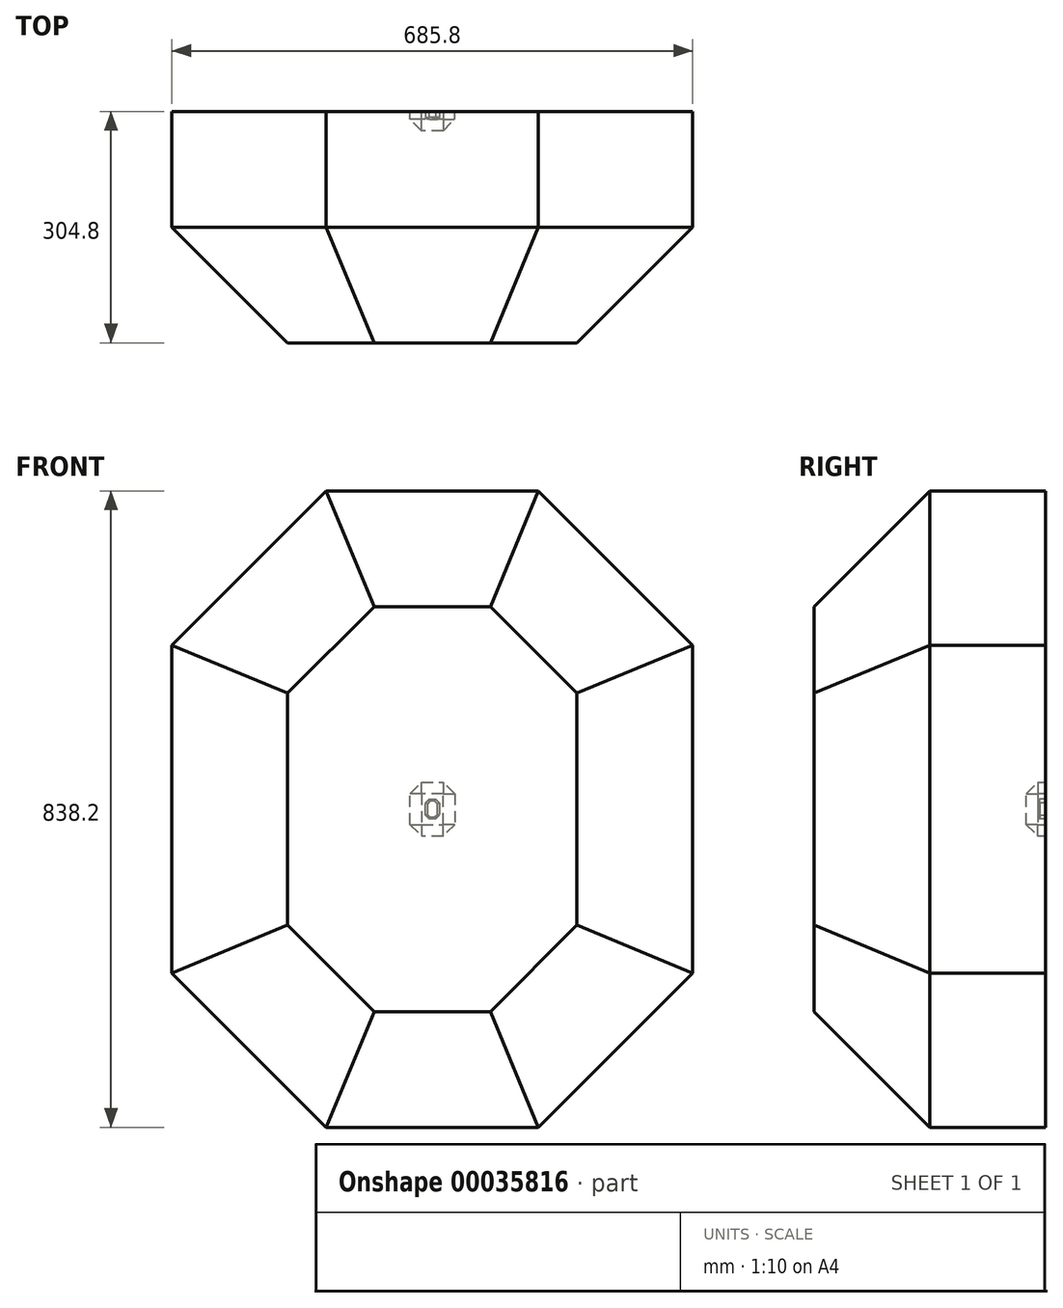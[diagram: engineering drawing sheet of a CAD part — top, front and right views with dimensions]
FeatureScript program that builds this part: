
annotation { "Feature Type Name" : "Feature", "Feature Type Description" : "" }
export const myFeature = defineFeature(function(context is Context, id is Id, definition is map)
    precondition{}
    {
        {
            var Q0;
            Q0=qCreatedBy(makeId("Front.planeOp"),FACE);
            var sketch = newSketch(context, id + "F0", { "sketchPlane" : qUnion([Q0])});
            skLineSegment(sketch, "E0.rect.bottom", {"start": v(29.36, -35.59) * mm, "end": v(-29.36, -35.59) * mm});
            skLineSegment(sketch, "E0.rect.top", {"start": v(29.36, 35.59) * mm, "end": v(-29.36, 35.59) * mm});
            skLineSegment(sketch, "E0.rect.left", {"start": v(29.36, -35.59) * mm, "end": v(29.36, 35.59) * mm});
            skLineSegment(sketch, "E0.rect.right", {"start": v(-29.36, -35.59) * mm, "end": v(-29.36, 35.59) * mm});
            skPoint(sketch, "E0.rect.middle", {"position": v(0, 0) * mm});
            skSolve(sketch);
        }
        {
            var Q0;
            Q0=makeQuery(id+"F0.imprint","IMPRINT",FACE,{"disambiguationData":[TD([[makeQuery(id+"F0.imprint","IMPRINT",EDGE,{"derivedFrom":sQuery(id+"F0.wireOp",EDGE,"E0.rect.bottom")}),-1.0]])]});
            extrude(context, id + "F1", {"entities" : qUnion([Q0]), "depth" : 25.4 * mm});
        }
        {
            var Q0;
            Q0=makeQuery(id+"F1.opExtrude","CAP_FACE",FACE,{"disambiguationData":[OSD([sQuery(id+"F0.wireOp",EDGE,"E0.rect.bottom"),sQuery(id+"F0.wireOp",EDGE,"E0.rect.top"),sQuery(id+"F0.wireOp",EDGE,"E0.rect.left"),sQuery(id+"F0.wireOp",EDGE,"E0.rect.right")])],"isStart":false});
            var Q1;
            Q1=makeQuery(id+"F1.opExtrude","SWEPT_EDGE",EDGE,{"disambiguationData":[OSD([sQuery(id+"F0.wireOp",EDGE,"E0.rect.bottom"),sQuery(id+"F0.wireOp",EDGE,"E0.rect.left")])]});
            var Q2;
            Q2=makeQuery(id+"F1.opExtrude","SWEPT_EDGE",EDGE,{"disambiguationData":[OSD([sQuery(id+"F0.wireOp",EDGE,"E0.rect.bottom"),sQuery(id+"F0.wireOp",EDGE,"E0.rect.right")])]});
            var Q3;
            Q3=makeQuery(id+"F1.opExtrude","SWEPT_EDGE",EDGE,{"disambiguationData":[OSD([sQuery(id+"F0.wireOp",EDGE,"E0.rect.top"),sQuery(id+"F0.wireOp",EDGE,"E0.rect.right")])]});
            var Q4;
            Q4=makeQuery(id+"F1.opExtrude","SWEPT_EDGE",EDGE,{"disambiguationData":[OSD([sQuery(id+"F0.wireOp",EDGE,"E0.rect.top"),sQuery(id+"F0.wireOp",EDGE,"E0.rect.left")])]});
            chamfer(context, id + "F2", {"entities" : qUnion([Q0, Q1, Q2, Q3, Q4]), "width" : 15.24 * mm, "tangentPropagation" : true});
        }
        {
            var Q0;
            Q0=qCreatedBy(makeId("Front.planeOp"),FACE);
            var sketch = newSketch(context, id + "F3", { "sketchPlane" : qUnion([Q0])});
            skLineSegment(sketch, "E1.rect.bottom", {"start": v(342.9, -419.1) * mm, "end": v(-342.9, -419.1) * mm});
            skLineSegment(sketch, "E1.rect.top", {"start": v(342.9, 419.1) * mm, "end": v(-342.9, 419.1) * mm});
            skLineSegment(sketch, "E1.rect.left", {"start": v(342.9, -419.1) * mm, "end": v(342.9, 419.1) * mm});
            skLineSegment(sketch, "E1.rect.right", {"start": v(-342.9, -419.1) * mm, "end": v(-342.9, 419.1) * mm});
            skPoint(sketch, "E1.rect.middle", {"position": v(0, 0) * mm});
            skSolve(sketch);
        }
        {
            var Q0;
            Q0=makeQuery(id+"F3.imprint","IMPRINT",FACE,{"disambiguationData":[TD([[makeQuery(id+"F3.imprint","IMPRINT",EDGE,{"derivedFrom":sQuery(id+"F3.wireOp",EDGE,"E1.rect.bottom")}),-1.0]])]});
            extrude(context, id + "F4", {"entities" : qUnion([Q0]), "depth" : 304.8 * mm});
        }
        {
            var Q0;
            Q0=makeQuery(id+"F4.opExtrude","SWEPT_EDGE",EDGE,{"disambiguationData":[OSD([sQuery(id+"F3.wireOp",EDGE,"E1.rect.top"),sQuery(id+"F3.wireOp",EDGE,"E1.rect.left")])]});
            var Q1;
            Q1=makeQuery(id+"F4.opExtrude","SWEPT_EDGE",EDGE,{"disambiguationData":[OSD([sQuery(id+"F3.wireOp",EDGE,"E1.rect.bottom"),sQuery(id+"F3.wireOp",EDGE,"E1.rect.left")])]});
            var Q2;
            Q2=makeQuery(id+"F4.opExtrude","SWEPT_EDGE",EDGE,{"disambiguationData":[OSD([sQuery(id+"F3.wireOp",EDGE,"E1.rect.bottom"),sQuery(id+"F3.wireOp",EDGE,"E1.rect.right")])]});
            var Q3;
            Q3=makeQuery(id+"F4.opExtrude","SWEPT_EDGE",EDGE,{"disambiguationData":[OSD([sQuery(id+"F3.wireOp",EDGE,"E1.rect.top"),sQuery(id+"F3.wireOp",EDGE,"E1.rect.right")])]});
            chamfer(context, id + "F5", {"entities" : qUnion([Q0, Q1, Q2, Q3]), "width" : 203.2 * mm, "tangentPropagation" : true});
        }
        {
            var Q0;
            Q0=makeQuery(id+"F4.opExtrude","CAP_FACE",FACE,{"disambiguationData":[OSD([sQuery(id+"F3.wireOp",EDGE,"E1.rect.bottom"),sQuery(id+"F3.wireOp",EDGE,"E1.rect.top"),sQuery(id+"F3.wireOp",EDGE,"E1.rect.left"),sQuery(id+"F3.wireOp",EDGE,"E1.rect.right")])],"isStart":false});
            chamfer(context, id + "F6", {"entities" : qUnion([Q0]), "width" : 152.4 * mm, "tangentPropagation" : true});
        }
        {
            var Q0;
            Q0=qCreatedBy(makeId("Front.planeOp"),FACE);
            var sketch = newSketch(context, id + "F7", { "sketchPlane" : qUnion([Q0])});
            skLineSegment(sketch, "E2.rect.bottom", {"start": v(9.3, -13.1) * mm, "end": v(-9.3, -13.1) * mm});
            skLineSegment(sketch, "E2.rect.top", {"start": v(9.3, 13.1) * mm, "end": v(-9.3, 13.1) * mm});
            skLineSegment(sketch, "E2.rect.left", {"start": v(9.3, -13.1) * mm, "end": v(9.3, 13.1) * mm});
            skLineSegment(sketch, "E2.rect.right", {"start": v(-9.3, -13.1) * mm, "end": v(-9.3, 13.1) * mm});
            skPoint(sketch, "E2.rect.middle", {"position": v(0, 0) * mm});
            skSolve(sketch);
        }
        {
            var Q0;
            Q0=makeQuery(id+"F7.imprint","IMPRINT",FACE,{"disambiguationData":[TD([[makeQuery(id+"F7.imprint","IMPRINT",EDGE,{"derivedFrom":sQuery(id+"F7.wireOp",EDGE,"E2.rect.bottom")}),-1.0]])]});
            extrude(context, id + "F8", {"entities" : qUnion([Q0]), "depth" : 10.16 * mm});
        }
        {
            var Q0;
            Q0=makeQuery(id+"F8.opExtrude","SWEPT_EDGE",EDGE,{"disambiguationData":[OSD([sQuery(id+"F7.wireOp",EDGE,"E2.rect.top"),sQuery(id+"F7.wireOp",EDGE,"E2.rect.right")])]});
            var Q1;
            Q1=makeQuery(id+"F8.opExtrude","SWEPT_EDGE",EDGE,{"disambiguationData":[OSD([sQuery(id+"F7.wireOp",EDGE,"E2.rect.top"),sQuery(id+"F7.wireOp",EDGE,"E2.rect.left")])]});
            var Q2;
            Q2=makeQuery(id+"F8.opExtrude","SWEPT_EDGE",EDGE,{"disambiguationData":[OSD([sQuery(id+"F7.wireOp",EDGE,"E2.rect.bottom"),sQuery(id+"F7.wireOp",EDGE,"E2.rect.right")])]});
            var Q3;
            Q3=makeQuery(id+"F8.opExtrude","SWEPT_EDGE",EDGE,{"disambiguationData":[OSD([sQuery(id+"F7.wireOp",EDGE,"E2.rect.bottom"),sQuery(id+"F7.wireOp",EDGE,"E2.rect.left")])]});
            chamfer(context, id + "F9", {"entities" : qUnion([Q0, Q1, Q2, Q3]), "width" : 5.08 * mm, "tangentPropagation" : true});
        }
        {
            var Q0;
            Q0=makeQuery(id+"F8.opExtrude","CAP_FACE",FACE,{"disambiguationData":[OSD([sQuery(id+"F7.wireOp",EDGE,"E2.rect.bottom"),sQuery(id+"F7.wireOp",EDGE,"E2.rect.top"),sQuery(id+"F7.wireOp",EDGE,"E2.rect.left"),sQuery(id+"F7.wireOp",EDGE,"E2.rect.right")])],"isStart":false});
            chamfer(context, id + "F10", {"entities" : qUnion([Q0]), "width" : 2.54 * mm, "tangentPropagation" : true});
        }
    });
